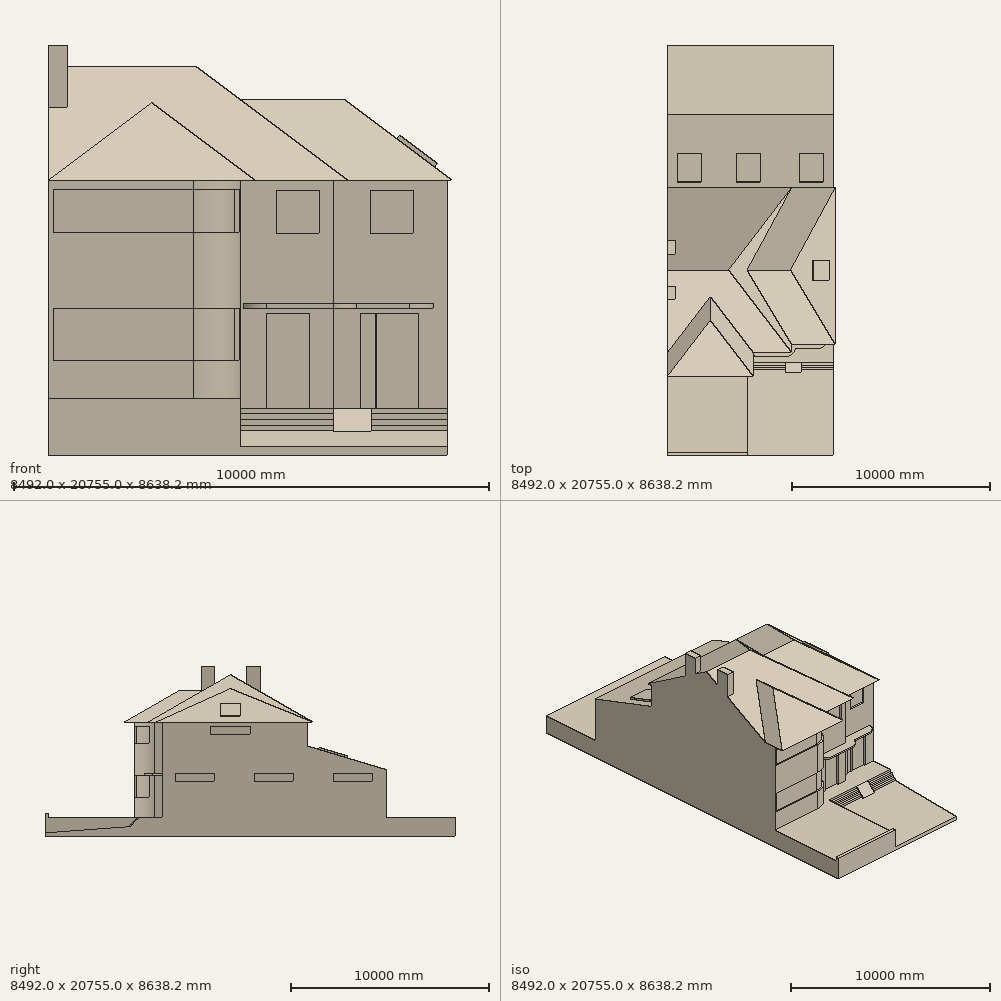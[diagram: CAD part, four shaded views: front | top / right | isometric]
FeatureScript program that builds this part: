
annotation { "Feature Type Name" : "Feature", "Feature Type Description" : "" }
export const myFeature = defineFeature(function(context is Context, id is Id, definition is map)
    precondition{}
    {
        {
            var Q0;
            Q0=qCreatedBy(makeId("Top.planeOp"),FACE);
            var sketch = newSketch(context, id + "F0", { "sketchPlane" : qUnion([Q0])});
            skLineSegment(sketch, "E0", {"start": v(0, -1400) * mm, "end": v(0, 11355) * mm});
            skLineSegment(sketch, "E1", {"start": v(0, 11355) * mm, "end": v(8392, 11355) * mm});
            skLineSegment(sketch, "E2", {"start": v(8392, 11355) * mm, "end": v(8392, 0) * mm});
            skLineSegment(sketch, "E3", {"start": v(8392, 0) * mm, "end": v(5992, 0) * mm});
            skLineSegment(sketch, "E4", {"start": v(5992, 0) * mm, "end": v(5992, -400) * mm});
            skLineSegment(sketch, "E5", {"start": v(5992, -400) * mm, "end": v(4042, -400) * mm});
            skLineSegment(sketch, "E6", {"start": v(0, -1400) * mm, "end": v(3042, -1400) * mm});
            skArc(sketch, "E7", {"start": v(3042, -1400) * mm, "mid": v(3749.1, -1107.1) * mm, "end": v(4042, -400) * mm});
            skSolve(sketch);
        }
        {
            var Q0;
            Q0=makeQuery(id+"F0.imprint","IMPRINT",FACE,{"disambiguationData":[TD([[makeQuery(id+"F0.imprint","IMPRINT",EDGE,{"derivedFrom":sQuery(id+"F0.wireOp",EDGE,"E0")}),-1.0]])]});
            extrude(context, id + "F1", {"entities" : qUnion([Q0]), "depth" : 4800 * mm});
        }
        {
            var Q0;
            Q0=makeQuery(id+"F1.opExtrude","CAP_FACE",FACE,{"disambiguationData":[OSD([sQuery(id+"F0.wireOp",EDGE,"E0"),sQuery(id+"F0.wireOp",EDGE,"E1"),sQuery(id+"F0.wireOp",EDGE,"E2"),sQuery(id+"F0.wireOp",EDGE,"E3"),sQuery(id+"F0.wireOp",EDGE,"E4"),sQuery(id+"F0.wireOp",EDGE,"E5"),sQuery(id+"F0.wireOp",EDGE,"E6"),sQuery(id+"F0.wireOp",EDGE,"E7")])],"isStart":false});
            var sketch = newSketch(context, id + "F2", { "sketchPlane" : qUnion([Q0])});
            skLineSegment(sketch, "E8.bottom", {"start": v(0, 11355) * mm, "end": v(8392, 11355) * mm});
            skLineSegment(sketch, "E8.top", {"start": v(0, 7355) * mm, "end": v(8392, 7355) * mm});
            skLineSegment(sketch, "E8.left", {"start": v(0, 11355) * mm, "end": v(0, 7355) * mm});
            skLineSegment(sketch, "E8.right", {"start": v(8392, 11355) * mm, "end": v(8392, 7355) * mm});
            skSolve(sketch);
        }
        {
            var Q0;
            Q0=makeQuery(id+"F2.imprint","IMPRINT",FACE,{"disambiguationData":[TD([[makeQuery(id+"F2.imprint","IMPRINT",EDGE,{"derivedFrom":sQuery(id+"F2.wireOp",EDGE,"E8.bottom")}),-1.0]])]});
            extrude(context, id + "F3", {"entities" : qUnion([Q0]), "operationType" : NewBodyOperationType.REMOVE, "oppositeDirection" : true, "depth" : 2400 * mm});
        }
        {
            var Q0;
            Q0=makeQuery(id+"F1.opExtrude","SWEPT_FACE",FACE,{"disambiguationData":[OSD([sQuery(id+"F0.wireOp",EDGE,"E2")])]});
            var sketch = newSketch(context, id + "F4", { "sketchPlane" : qUnion([Q0])});
            skLineSegment(sketch, "E9", {"start": v(11355, 2400) * mm, "end": v(7355, 3600) * mm});
            skLineSegment(sketch, "E10", {"start": v(7355, 3600) * mm, "end": v(7355, 2400) * mm});
            skLineSegment(sketch, "E11", {"start": v(7355, 2400) * mm, "end": v(11355, 2400) * mm});
            skSolve(sketch);
        }
        {
            var Q0;
            Q0=makeQuery(id+"F4.imprint","IMPRINT",FACE,{"disambiguationData":[TD([[makeQuery(id+"F4.imprint","IMPRINT",EDGE,{"derivedFrom":sQuery(id+"F4.wireOp",EDGE,"E9")}),1.0]])]});
            var Q1;
            Q1=makeQuery(id+"F1.opExtrude","SWEPT_FACE",FACE,{"disambiguationData":[OSD([sQuery(id+"F0.wireOp",EDGE,"E0")])]});
            extrude(context, id + "F5", {"entities" : qUnion([Q0]), "operationType" : NewBodyOperationType.ADD, "endBound" : BoundingType.UP_TO_SURFACE, "oppositeDirection" : true, "endBoundEntityFace" : qUnion([Q1]), "depth" : 25 * mm});
        }
        {
            var Q0;
            Q0=makeQuery(id+"F1.opExtrude","SWEPT_FACE",FACE,{"disambiguationData":[OSD([sQuery(id+"F0.wireOp",EDGE,"E4")])]});
            var sketch = newSketch(context, id + "F6", { "sketchPlane" : qUnion([Q0])});
            skLineSegment(sketch, "E12", {"start": v(-700, 4800) * mm, "end": v(3477.5, 7200) * mm});
            skLineSegment(sketch, "E13", {"start": v(3477.5, 7200) * mm, "end": v(7655, 4800) * mm});
            skLineSegment(sketch, "E14", {"start": v(7655, 4800) * mm, "end": v(-700, 4800) * mm});
            skSolve(sketch);
        }
        {
            var Q0;
            {var subQ0=sQuery(id+"F6.wireOp",EDGE,"E12");Q0=makeQuery(id+"F6.imprint","IMPRINT",FACE,{"disambiguationData":[TD([[makeQuery(id+"F6.imprint","IMPRINT",EDGE,{"derivedFrom":subQ0}),-1.0]])]});}
            var Q1;
            {var subQ0=sQuery(id+"F0.wireOp",EDGE,"E0");Q1=makeQuery(id+"F5.boolean.opBoolean","MERGE",FACE,{"derivedFrom":[makeQuery(id+"F1.opExtrude","SWEPT_FACE",FACE,{"disambiguationData":[OSD([subQ0])]}),makeQuery(id+"F5.opExtrude","CAP_FACE",FACE,{"disambiguationData":[OSD([subQ0])],"isStart":false})]});}
            extrude(context, id + "F7", {"entities" : qUnion([Q0]), "operationType" : NewBodyOperationType.ADD, "endBound" : BoundingType.UP_TO_SURFACE, "oppositeDirection" : true, "endBoundEntityFace" : qUnion([Q1]), "depth" : 25 * mm});
        }
        {
            var Q0;
            Q0 = qSketchRegion(id + "F6", true);
            extrude(context, id + "F8", {"entities" : qUnion([Q0]), "operationType" : NewBodyOperationType.ADD, "depth" : 300 * mm});
        }
        {
            var Q0;
            Q0=makeQuery(id+"F5.boolean.opBoolean","MERGE",FACE,{"derivedFrom":[makeQuery(id+"F1.opExtrude","SWEPT_FACE",FACE,{"disambiguationData":[OSD([sQuery(id+"F0.wireOp",EDGE,"E2")])]}),makeQuery(id+"F5.opExtrude","CAP_FACE",FACE,{"disambiguationData":[OSD([sQuery(id+"F4.wireOp",EDGE,"E9"),sQuery(id+"F4.wireOp",EDGE,"E10"),sQuery(id+"F4.wireOp",EDGE,"E11")])],"isStart":true})]});
            var sketch = newSketch(context, id + "F9", { "sketchPlane" : qUnion([Q0])});
            skLineSegment(sketch, "E15", {"start": v(-300, 4800) * mm, "end": v(3477.5, 6500) * mm});
            skLineSegment(sketch, "E16", {"start": v(3477.5, 6500) * mm, "end": v(7655, 4800) * mm});
            skLineSegment(sketch, "E17", {"start": v(7655, 4800) * mm, "end": v(-300, 4800) * mm});
            skLineSegment(sketch, "E18", {"start": v(3477.5, 6500) * mm, "end": v(3477.5, 7200) * mm, "construction": true});
            skSolve(sketch);
        }
        {
            var Q0;
            Q0=makeQuery(id+"F1.opExtrude","SWEPT_FACE",FACE,{"disambiguationData":[OSD([sQuery(id+"F0.wireOp",EDGE,"E6")])]});
            var sketch = newSketch(context, id + "F10", { "sketchPlane" : qUnion([Q0])});
            skLineSegment(sketch, "E19", {"start": v(6292, 4800) * mm, "end": v(2292, 7800) * mm});
            skLineSegment(sketch, "E20", {"start": v(2292, 7800) * mm, "end": v(6292, 7800) * mm});
            skLineSegment(sketch, "E21", {"start": v(6292, 7800) * mm, "end": v(6292, 4800) * mm});
            skSolve(sketch);
        }
        {
            var Q0;
            Q0=makeQuery(id+"F10.imprint","IMPRINT",FACE,{"disambiguationData":[TD([[makeQuery(id+"F10.imprint","IMPRINT",EDGE,{"derivedFrom":sQuery(id+"F10.wireOp",EDGE,"E19")}),-1.0]])]});
            extrude(context, id + "F11", {"entities" : qUnion([Q0]), "operationType" : NewBodyOperationType.REMOVE, "endBound" : BoundingType.THROUGH_ALL, "oppositeDirection" : true, "depth" : 25 * mm});
        }
        {
            var Q0;
            Q0=makeQuery(id+"F1.opExtrude","SWEPT_FACE",FACE,{"disambiguationData":[OSD([sQuery(id+"F0.wireOp",EDGE,"E6")])]});
            var sketch = newSketch(context, id + "F12", { "sketchPlane" : qUnion([Q0])});
            skLineSegment(sketch, "E22", {"start": v(0, 4800) * mm, "end": v(2171, 6428.25) * mm});
            skLineSegment(sketch, "E23", {"start": v(2171, 6428.25) * mm, "end": v(4342, 4800) * mm});
            skLineSegment(sketch, "E24", {"start": v(4342, 4800) * mm, "end": v(0, 4800) * mm});
            skSolve(sketch);
        }
        {
            var Q0;
            {var subQ6=sQuery(id+"F12.wireOp",EDGE,"E22");Q0=makeQuery(id+"F12.imprint","IMPRINT",FACE,{"disambiguationData":[TD([[makeQuery(id+"F12.imprint","IMPRINT",EDGE,{"derivedFrom":subQ6}),-1.0]])]});}
            extrude(context, id + "F13", {"entities" : qUnion([Q0]), "operationType" : NewBodyOperationType.ADD, "endBound" : BoundingType.UP_TO_NEXT, "oppositeDirection" : true, "depth" : 25 * mm});
        }
        {
            var Q0;
            Q0 = qSketchRegion(id + "F12", true);
            extrude(context, id + "F14", {"entities" : qUnion([Q0]), "operationType" : NewBodyOperationType.ADD, "depth" : 500 * mm});
        }
        {
            var Q0;
            {var subQ0=sQuery(id+"F0.wireOp",EDGE,"E0");Q0=makeQuery(id+"F7.boolean.opBoolean","MERGE",FACE,{"derivedFrom":[makeQuery(id+"F5.boolean.opBoolean","MERGE",FACE,{"derivedFrom":[makeQuery(id+"F1.opExtrude","SWEPT_FACE",FACE,{"disambiguationData":[OSD([subQ0])]}),makeQuery(id+"F5.opExtrude","CAP_FACE",FACE,{"disambiguationData":[OSD([subQ0])],"isStart":false})]}),makeQuery(id+"F7.opExtrude","CAP_FACE",FACE,{"disambiguationData":[OSD([subQ0])],"isStart":false})]});}
            var sketch = newSketch(context, id + "F15", { "sketchPlane" : qUnion([Q0])});
            skLineSegment(sketch, "E25", {"start": v(1900, 4800) * mm, "end": v(1900, 6428.25) * mm});
            skLineSegment(sketch, "E26", {"start": v(-934.17, 6428.25) * mm, "end": v(1900, 6428.25) * mm});
            skLineSegment(sketch, "E27", {"start": v(1900, 4800) * mm, "end": v(-934.17, 6428.25) * mm});
            skSolve(sketch);
        }
        {
            var Q0;
            Q0=makeQuery(id+"F15.imprint","IMPRINT",FACE,{"disambiguationData":[TD([[makeQuery(id+"F15.imprint","IMPRINT",EDGE,{"derivedFrom":sQuery(id+"F15.wireOp",EDGE,"E25")}),-1.0]])]});
            var Q1;
            Q1=makeQuery(id+"F15.imprint","IMPRINT",FACE,{"disambiguationData":[TD([[makeQuery(id+"F15.imprint","IMPRINT",EDGE,{"derivedFrom":sQuery(id+"F15.wireOp",EDGE,"E25")}),1.0]])]});
            extrude(context, id + "F16", {"entities" : qUnion([Q0, Q1]), "operationType" : NewBodyOperationType.REMOVE, "endBound" : BoundingType.THROUGH_ALL, "oppositeDirection" : true, "depth" : 25 * mm});
        }
        {
            var Q0;
            Q0=makeQuery(id+"F9.imprint","IMPRINT",FACE,{"disambiguationData":[TD([[makeQuery(id+"F9.imprint","IMPRINT",EDGE,{"derivedFrom":sQuery(id+"F9.wireOp",EDGE,"E15")}),-1.0]])]});
            extrude(context, id + "F17", {"entities" : qUnion([Q0]), "operationType" : NewBodyOperationType.ADD, "endBound" : BoundingType.UP_TO_NEXT, "oppositeDirection" : true, "depth" : 25 * mm});
        }
        {
            var Q0;
            Q0 = qSketchRegion(id + "F9", true);
            extrude(context, id + "F18", {"entities" : qUnion([Q0]), "operationType" : NewBodyOperationType.ADD, "depth" : 100 * mm});
        }
        {
            var Q0;
            Q0=makeQuery(id+"F13.boolean.opBoolean","MERGE",FACE,{"derivedFrom":[makeQuery(id+"F1.opExtrude","SWEPT_FACE",FACE,{"disambiguationData":[OSD([sQuery(id+"F0.wireOp",EDGE,"E6")])]}),makeQuery(id+"F13.opExtrude","CAP_FACE",FACE,{"disambiguationData":[OSD([sQuery(id+"F12.wireOp",EDGE,"E22"),sQuery(id+"F12.wireOp",EDGE,"E23"),sQuery(id+"F12.wireOp",EDGE,"E24")])],"isStart":true})]});
            var sketch = newSketch(context, id + "F19", { "sketchPlane" : qUnion([Q0])});
            skLineSegment(sketch, "E28", {"start": v(8492, 4800) * mm, "end": v(6225.33, 6500) * mm});
            skLineSegment(sketch, "E29", {"start": v(6225.33, 6500) * mm, "end": v(8492, 6500) * mm});
            skLineSegment(sketch, "E30", {"start": v(8492, 6500) * mm, "end": v(8492, 4800) * mm});
            skSolve(sketch);
        }
        {
            var Q0;
            Q0=makeQuery(id+"F19.imprint","IMPRINT",FACE,{"disambiguationData":[TD([[makeQuery(id+"F19.imprint","IMPRINT",EDGE,{"derivedFrom":sQuery(id+"F19.wireOp",EDGE,"E28")}),-1.0]])]});
            extrude(context, id + "F20", {"entities" : qUnion([Q0]), "operationType" : NewBodyOperationType.REMOVE, "endBound" : BoundingType.THROUGH_ALL, "oppositeDirection" : true, "depth" : 25 * mm});
        }
        {
            var Q0;
            Q0=makeQuery(id+"F17.boolean.opBoolean","MERGE",FACE,{"derivedFrom":[makeQuery(id+"F5.boolean.opBoolean","MERGE",FACE,{"derivedFrom":[makeQuery(id+"F1.opExtrude","SWEPT_FACE",FACE,{"disambiguationData":[OSD([sQuery(id+"F0.wireOp",EDGE,"E2")])]}),makeQuery(id+"F5.opExtrude","CAP_FACE",FACE,{"disambiguationData":[OSD([sQuery(id+"F4.wireOp",EDGE,"E9"),sQuery(id+"F4.wireOp",EDGE,"E10"),sQuery(id+"F4.wireOp",EDGE,"E11")])],"isStart":true})]}),makeQuery(id+"F17.opExtrude","CAP_FACE",FACE,{"disambiguationData":[OSD([sQuery(id+"F9.wireOp",EDGE,"E15"),sQuery(id+"F9.wireOp",EDGE,"E16"),sQuery(id+"F9.wireOp",EDGE,"E17")])],"isStart":true})]});
            var sketch = newSketch(context, id + "F21", { "sketchPlane" : qUnion([Q0])});
            skLineSegment(sketch, "E31.bottom", {"start": v(2477.5, 4600) * mm, "end": v(4477.5, 4600) * mm});
            skLineSegment(sketch, "E31.top", {"start": v(2477.5, 4200) * mm, "end": v(4477.5, 4200) * mm});
            skLineSegment(sketch, "E31.left", {"start": v(2477.5, 4600) * mm, "end": v(2477.5, 4200) * mm});
            skLineSegment(sketch, "E31.right", {"start": v(4477.5, 4600) * mm, "end": v(4477.5, 4200) * mm});
            skLineSegment(sketch, "E32", {"start": v(3477.5, 7200) * mm, "end": v(3477.5, 0) * mm, "construction": true});
            skPoint(sketch, "E33", {"position": v(3477.5, 4600) * mm});
            skLineSegment(sketch, "E34.bottom", {"start": v(677.5, 2200) * mm, "end": v(2677.5, 2200) * mm});
            skLineSegment(sketch, "E34.top", {"start": v(677.5, 1800) * mm, "end": v(2677.5, 1800) * mm});
            skLineSegment(sketch, "E34.left", {"start": v(677.5, 2200) * mm, "end": v(677.5, 1800) * mm});
            skLineSegment(sketch, "E34.right", {"start": v(2677.5, 2200) * mm, "end": v(2677.5, 1800) * mm});
            skLineSegment(sketch, "E35.bottom", {"start": v(4677.5, 2200) * mm, "end": v(6677.5, 2200) * mm});
            skLineSegment(sketch, "E35.top", {"start": v(4677.5, 1800) * mm, "end": v(6677.5, 1800) * mm});
            skLineSegment(sketch, "E35.left", {"start": v(4677.5, 2200) * mm, "end": v(4677.5, 1800) * mm});
            skLineSegment(sketch, "E35.right", {"start": v(6677.5, 2200) * mm, "end": v(6677.5, 1800) * mm});
            skLineSegment(sketch, "E36.bottom", {"start": v(8677.5, 2200) * mm, "end": v(10677.5, 2200) * mm});
            skLineSegment(sketch, "E36.top", {"start": v(8677.5, 1800) * mm, "end": v(10677.5, 1800) * mm});
            skLineSegment(sketch, "E36.left", {"start": v(8677.5, 2200) * mm, "end": v(8677.5, 1800) * mm});
            skLineSegment(sketch, "E36.right", {"start": v(10677.5, 2200) * mm, "end": v(10677.5, 1800) * mm});
            skSolve(sketch);
        }
        {
            var Q0;
            Q0=makeQuery(id+"F21.imprint","IMPRINT",FACE,{"disambiguationData":[TD([[makeQuery(id+"F21.imprint","IMPRINT",EDGE,{"derivedFrom":sQuery(id+"F21.wireOp",EDGE,"E35.bottom")}),-1.0]])]});
            var Q1;
            Q1=makeQuery(id+"F21.imprint","IMPRINT",FACE,{"disambiguationData":[TD([[makeQuery(id+"F21.imprint","IMPRINT",EDGE,{"derivedFrom":sQuery(id+"F21.wireOp",EDGE,"E34.bottom")}),-1.0]])]});
            var Q2;
            Q2=makeQuery(id+"F21.imprint","IMPRINT",FACE,{"disambiguationData":[TD([[makeQuery(id+"F21.imprint","IMPRINT",EDGE,{"derivedFrom":sQuery(id+"F21.wireOp",EDGE,"E31.bottom")}),-1.0]])]});
            var Q3;
            Q3=makeQuery(id+"F21.imprint","IMPRINT",FACE,{"disambiguationData":[TD([[makeQuery(id+"F21.imprint","IMPRINT",EDGE,{"derivedFrom":sQuery(id+"F21.wireOp",EDGE,"E36.bottom")}),-1.0]])]});
            extrude(context, id + "F22", {"entities" : qUnion([Q0, Q1, Q2, Q3]), "operationType" : NewBodyOperationType.REMOVE, "oppositeDirection" : true, "depth" : 100 * mm});
        }
        {
            var Q0;
            Q0=makeQuery(id+"F1.opExtrude","SWEPT_FACE",FACE,{"disambiguationData":[OSD([sQuery(id+"F0.wireOp",EDGE,"E3")])]});
            var sketch = newSketch(context, id + "F23", { "sketchPlane" : qUnion([Q0])});
            skLineSegment(sketch, "E37.bottom", {"start": v(6892, 0) * mm, "end": v(7792, 0) * mm});
            skLineSegment(sketch, "E37.top", {"start": v(6892, 2000) * mm, "end": v(7792, 2000) * mm});
            skLineSegment(sketch, "E37.left", {"start": v(6892, 0) * mm, "end": v(6892, 2000) * mm});
            skLineSegment(sketch, "E37.right", {"start": v(7792, 0) * mm, "end": v(7792, 2000) * mm});
            skLineSegment(sketch, "E38.bottom", {"start": v(6872, 0) * mm, "end": v(6572, 0) * mm});
            skLineSegment(sketch, "E38.top", {"start": v(6872, 2000) * mm, "end": v(6572, 2000) * mm});
            skLineSegment(sketch, "E38.left", {"start": v(6872, 0) * mm, "end": v(6872, 2000) * mm});
            skLineSegment(sketch, "E38.right", {"start": v(6572, 0) * mm, "end": v(6572, 2000) * mm});
            skLineSegment(sketch, "E39.bottom", {"start": v(6783.06, 4584.82) * mm, "end": v(7683.06, 4584.82) * mm});
            skLineSegment(sketch, "E39.top", {"start": v(6783.06, 3684.82) * mm, "end": v(7683.06, 3684.82) * mm});
            skLineSegment(sketch, "E39.left", {"start": v(6783.06, 4584.82) * mm, "end": v(6783.06, 3684.82) * mm});
            skLineSegment(sketch, "E39.right", {"start": v(7683.06, 4584.82) * mm, "end": v(7683.06, 3684.82) * mm});
            skLineSegment(sketch, "E40", {"start": v(7233.06, 4800) * mm, "end": v(7233.06, 4584.82) * mm, "construction": true});
            skPoint(sketch, "E40.startSnap0", {"position": v(7233.06, 4584.82) * mm});
            skSolve(sketch);
        }
        {
            var Q0;
            Q0=makeQuery(id+"F23.imprint","IMPRINT",FACE,{"disambiguationData":[TD([[makeQuery(id+"F23.imprint","IMPRINT",EDGE,{"derivedFrom":sQuery(id+"F23.wireOp",EDGE,"E39.bottom")}),-1.0]])]});
            var Q1;
            Q1=makeQuery(id+"F23.imprint","IMPRINT",FACE,{"disambiguationData":[TD([[makeQuery(id+"F23.imprint","IMPRINT",EDGE,{"derivedFrom":sQuery(id+"F23.wireOp",EDGE,"E37.bottom")}),-1.0]])]});
            var Q2;
            Q2=makeQuery(id+"F23.imprint","IMPRINT",FACE,{"disambiguationData":[TD([[makeQuery(id+"F23.imprint","IMPRINT",EDGE,{"derivedFrom":sQuery(id+"F23.wireOp",EDGE,"E38.bottom")}),-1.0]])]});
            extrude(context, id + "F24", {"entities" : qUnion([Q0, Q1, Q2]), "operationType" : NewBodyOperationType.REMOVE, "oppositeDirection" : true, "depth" : 100 * mm});
        }
        {
            var Q0;
            Q0=makeQuery(id+"F1.opExtrude","SWEPT_FACE",FACE,{"disambiguationData":[OSD([sQuery(id+"F0.wireOp",EDGE,"E5")])]});
            var sketch = newSketch(context, id + "F25", { "sketchPlane" : qUnion([Q0])});
            skLineSegment(sketch, "E41.bottom", {"start": v(4592, 0) * mm, "end": v(5492, 0) * mm});
            skLineSegment(sketch, "E41.top", {"start": v(4592, 2000) * mm, "end": v(5492, 2000) * mm});
            skLineSegment(sketch, "E41.left", {"start": v(4592, 0) * mm, "end": v(4592, 2000) * mm});
            skLineSegment(sketch, "E41.right", {"start": v(5492, 0) * mm, "end": v(5492, 2000) * mm});
            skLineSegment(sketch, "E42.bottom", {"start": v(4792, 4584.82) * mm, "end": v(5692, 4584.82) * mm});
            skLineSegment(sketch, "E42.top", {"start": v(4792, 3684.82) * mm, "end": v(5692, 3684.82) * mm});
            skLineSegment(sketch, "E42.left", {"start": v(4792, 4584.82) * mm, "end": v(4792, 3684.82) * mm});
            skLineSegment(sketch, "E42.right", {"start": v(5692, 4584.82) * mm, "end": v(5692, 3684.82) * mm});
            skSolve(sketch);
        }
        {
            var Q0;
            Q0=makeQuery(id+"F25.imprint","IMPRINT",FACE,{"disambiguationData":[TD([[makeQuery(id+"F25.imprint","IMPRINT",EDGE,{"derivedFrom":sQuery(id+"F25.wireOp",EDGE,"E41.bottom")}),-1.0]])]});
            var Q1;
            Q1=makeQuery(id+"F25.imprint","IMPRINT",FACE,{"disambiguationData":[TD([[makeQuery(id+"F25.imprint","IMPRINT",EDGE,{"derivedFrom":sQuery(id+"F25.wireOp",EDGE,"E42.bottom")}),-1.0]])]});
            extrude(context, id + "F26", {"entities" : qUnion([Q0, Q1]), "operationType" : NewBodyOperationType.REMOVE, "oppositeDirection" : true, "depth" : 100 * mm});
        }
        {
            var Q0;
            Q0=makeQuery(id+"F1.opExtrude","CAP_FACE",FACE,{"disambiguationData":[OSD([sQuery(id+"F0.wireOp",EDGE,"E0"),sQuery(id+"F0.wireOp",EDGE,"E1"),sQuery(id+"F0.wireOp",EDGE,"E2"),sQuery(id+"F0.wireOp",EDGE,"E3"),sQuery(id+"F0.wireOp",EDGE,"E4"),sQuery(id+"F0.wireOp",EDGE,"E5"),sQuery(id+"F0.wireOp",EDGE,"E6"),sQuery(id+"F0.wireOp",EDGE,"E7")])],"isStart":true});
            cPlane(context, id + "F27", {"entities" : qUnion([Q0]), "cplaneType" : CPlaneType.OFFSET, "offset" : 1000 * mm, "oppositeDirection" : true, "width" : 150 * mm, "height" : 150 * mm});
        }
        {
            var Q0;
            Q0=qCreatedBy(id+"F27.planeOp",FACE);
            var sketch = newSketch(context, id + "F28", { "sketchPlane" : qUnion([Q0])});
            skLineSegment(sketch, "E43", {"start": v(100, 1400) * mm, "end": v(100, 1300) * mm});
            skLineSegment(sketch, "E44", {"start": v(100, 1300) * mm, "end": v(3042, 1300) * mm});
            skArc(sketch, "E45", {"start": v(3913.42, 624.99) * mm, "mid": v(3593.14, 1111.5) * mm, "end": v(3042, 1300) * mm});
            skArc(sketch, "E46", {"start": v(4016.36, 624.99) * mm, "mid": v(3664.5, 1182.62) * mm, "end": v(3042, 1400) * mm});
            skLineSegment(sketch, "E47", {"start": v(100, 1400) * mm, "end": v(3042, 1400) * mm});
            skLineSegment(sketch, "E48", {"start": v(3913.42, 624.99) * mm, "end": v(4016.36, 624.99) * mm});
            skSolve(sketch);
        }
        {
            var Q0;
            Q0 = qSketchRegion(id + "F28", true);
            extrude(context, id + "F29", {"entities" : qUnion([Q0]), "operationType" : NewBodyOperationType.REMOVE, "oppositeDirection" : true, "depth" : 1100 * mm});
        }
        {
            var Q0;
            Q0=makeQuery(id+"F1.opExtrude","CAP_FACE",FACE,{"disambiguationData":[OSD([sQuery(id+"F0.wireOp",EDGE,"E0"),sQuery(id+"F0.wireOp",EDGE,"E1"),sQuery(id+"F0.wireOp",EDGE,"E2"),sQuery(id+"F0.wireOp",EDGE,"E3"),sQuery(id+"F0.wireOp",EDGE,"E4"),sQuery(id+"F0.wireOp",EDGE,"E5"),sQuery(id+"F0.wireOp",EDGE,"E6"),sQuery(id+"F0.wireOp",EDGE,"E7")])],"isStart":true});
            cPlane(context, id + "F30", {"entities" : qUnion([Q0]), "cplaneType" : CPlaneType.OFFSET, "offset" : 3700 * mm, "oppositeDirection" : true, "width" : 150 * mm, "height" : 150 * mm});
        }
        {
            var Q0;
            Q0=qCreatedBy(id+"F30.planeOp",FACE);
            var sketch = newSketch(context, id + "F31", { "sketchPlane" : qUnion([Q0])});
            skLineSegment(sketch, "E49.0", {"start": v(100, 1300) * mm, "end": v(3042, 1300) * mm});
            skArc(sketch, "E49.1", {"start": v(3913.42, 624.99) * mm, "mid": v(3593.14, 1111.5) * mm, "end": v(3042, 1300) * mm});
            skLineSegment(sketch, "E49.2", {"start": v(3913.42, 624.99) * mm, "end": v(4016.36, 624.99) * mm});
            skLineSegment(sketch, "E50.0", {"start": v(100, 1400) * mm, "end": v(100, 1300) * mm});
            skLineSegment(sketch, "E51.0", {"start": v(100, 1400) * mm, "end": v(3042, 1400) * mm});
            skArc(sketch, "E51.1", {"start": v(3042, 1400) * mm, "mid": v(3664.5, 1182.62) * mm, "end": v(4016.36, 624.99) * mm});
            skPoint(sketch, "E52.orphan", {"position": v(4042, 400) * mm});
            skPoint(sketch, "E53.orphan", {"position": v(0, 1400) * mm});
            skSolve(sketch);
        }
        {
            var Q0;
            Q0 = qSketchRegion(id + "F31", true);
            extrude(context, id + "F32", {"entities" : qUnion([Q0]), "operationType" : NewBodyOperationType.REMOVE, "oppositeDirection" : true, "depth" : 900 * mm});
        }
        {
            var Q0;
            Q0=makeQuery(id+"F29.boolean.opBoolean","COPY",FACE,{"derivedFrom":makeQuery(id+"F29.opExtrude","CAP_FACE",FACE,{"disambiguationData":[OSD([sQuery(id+"F28.wireOp",EDGE,"E43"),sQuery(id+"F28.wireOp",EDGE,"E44"),sQuery(id+"F28.wireOp",EDGE,"E45"),sQuery(id+"F28.wireOp",EDGE,"E46"),sQuery(id+"F28.wireOp",EDGE,"E47"),sQuery(id+"F28.wireOp",EDGE,"E48")])],"isStart":false})});
            var sketch = newSketch(context, id + "F33", { "sketchPlane" : qUnion([Q0])});
            skLineSegment(sketch, "E54", {"start": v(8092, 500) * mm, "end": v(8092, 0) * mm});
            skLineSegment(sketch, "E55", {"start": v(8092, 0) * mm, "end": v(5992, 0) * mm});
            skLineSegment(sketch, "E56", {"start": v(5992, 0) * mm, "end": v(5992, 400) * mm});
            skLineSegment(sketch, "E57", {"start": v(5992, 400) * mm, "end": v(4092, 400) * mm});
            skLineSegment(sketch, "E58", {"start": v(4092, 400) * mm, "end": v(4092, 900) * mm});
            skLineSegment(sketch, "E59", {"start": v(4092, 900) * mm, "end": v(5992, 900) * mm});
            skLineSegment(sketch, "E60", {"start": v(6481.9, 500) * mm, "end": v(8092, 500) * mm});
            skArc(sketch, "E61", {"start": v(6481.9, 500) * mm, "mid": v(6308.23, 787.3) * mm, "end": v(5992, 900) * mm});
            skSolve(sketch);
        }
        {
            var Q0;
            Q0=makeQuery(id+"F33.imprint","IMPRINT",FACE,{"disambiguationData":[TD([[makeQuery(id+"F33.imprint","IMPRINT",EDGE,{"derivedFrom":sQuery(id+"F33.wireOp",EDGE,"E54")}),-1.0]])]});
            extrude(context, id + "F34", {"entities" : qUnion([Q0]), "operationType" : NewBodyOperationType.ADD, "oppositeDirection" : true, "depth" : 100 * mm});
        }
        {
            var Q0;
            {var subQ0=sQuery(id+"F0.wireOp",EDGE,"E0");Q0=makeQuery(id+"F7.boolean.opBoolean","MERGE",FACE,{"derivedFrom":[makeQuery(id+"F5.boolean.opBoolean","MERGE",FACE,{"derivedFrom":[makeQuery(id+"F1.opExtrude","SWEPT_FACE",FACE,{"disambiguationData":[OSD([subQ0])]}),makeQuery(id+"F5.opExtrude","CAP_FACE",FACE,{"disambiguationData":[OSD([subQ0])],"isStart":false})]}),makeQuery(id+"F7.opExtrude","CAP_FACE",FACE,{"disambiguationData":[OSD([subQ0])],"isStart":false})]});}
            var sketch = newSketch(context, id + "F35", { "sketchPlane" : qUnion([Q0])});
            skLineSegment(sketch, "E62.bottom", {"start": v(-1977.5, 6338.24) * mm, "end": v(-2677.5, 6338.24) * mm});
            skLineSegment(sketch, "E62.top", {"start": v(-1977.5, 7638.24) * mm, "end": v(-2677.5, 7638.24) * mm});
            skLineSegment(sketch, "E62.left", {"start": v(-1977.5, 6338.24) * mm, "end": v(-1977.5, 7638.24) * mm});
            skLineSegment(sketch, "E62.right", {"start": v(-2677.5, 6338.24) * mm, "end": v(-2677.5, 7638.24) * mm});
            skLineSegment(sketch, "E63.bottom", {"start": v(-4977.5, 6338.24) * mm, "end": v(-4277.5, 6338.24) * mm});
            skLineSegment(sketch, "E63.top", {"start": v(-4977.5, 7638.24) * mm, "end": v(-4277.5, 7638.24) * mm});
            skLineSegment(sketch, "E63.left", {"start": v(-4977.5, 6338.24) * mm, "end": v(-4977.5, 7638.24) * mm});
            skLineSegment(sketch, "E63.right", {"start": v(-4277.5, 6338.24) * mm, "end": v(-4277.5, 7638.24) * mm});
            skSolve(sketch);
        }
        {
            var Q0;
            {var subQ0=sQuery(id+"F35.wireOp",EDGE,"E62.top");Q0=makeQuery(id+"F35.imprint","IMPRINT",FACE,{"disambiguationData":[TD([[makeQuery(id+"F35.imprint","IMPRINT",EDGE,{"derivedFrom":subQ0}),1.0]])]});}
            var Q1;
            {var subQ0=sQuery(id+"F35.wireOp",EDGE,"E63.top");Q1=makeQuery(id+"F35.imprint","IMPRINT",FACE,{"disambiguationData":[TD([[makeQuery(id+"F35.imprint","IMPRINT",EDGE,{"derivedFrom":subQ0}),-1.0]])]});}
            extrude(context, id + "F36", {"entities" : qUnion([Q0, Q1]), "operationType" : NewBodyOperationType.ADD, "oppositeDirection" : true, "depth" : 400 * mm});
        }
        {
            var Q0;
            Q0=makeQuery(id+"F34.opExtrude","SWEPT_EDGE",EDGE,{"disambiguationData":[OSD([sQuery(id+"F33.wireOp",EDGE,"E54"),sQuery(id+"F33.wireOp",EDGE,"E60")])]});
            var Q1;
            Q1=makeQuery(id+"F34.opExtrude","SWEPT_EDGE",EDGE,{"disambiguationData":[OSD([sQuery(id+"F33.wireOp",EDGE,"E58"),sQuery(id+"F33.wireOp",EDGE,"E59")])]});
            fillet(context, id + "F37", {"entities" : qUnion([Q0, Q1]), "radius" : 500 * mm, "tangentPropagation" : true, "allowEdgeOverflow" : false});
        }
        {
            var Q0;
            Q0=makeQuery(id+"F1.opExtrude","SWEPT_FACE",FACE,{"disambiguationData":[OSD([sQuery(id+"F0.wireOp",EDGE,"E1")])]});
            var sketch = newSketch(context, id + "F38", { "sketchPlane" : qUnion([Q0])});
            skLineSegment(sketch, "E64.bottom", {"start": v(-8152, 0) * mm, "end": v(-6252, 0) * mm});
            skLineSegment(sketch, "E64.top", {"start": v(-8152, 2300) * mm, "end": v(-6252, 2300) * mm});
            skLineSegment(sketch, "E64.left", {"start": v(-8152, 0) * mm, "end": v(-8152, 2300) * mm});
            skLineSegment(sketch, "E64.right", {"start": v(-6252, 0) * mm, "end": v(-6252, 2300) * mm});
            skSolve(sketch);
        }
        {
            var Q0;
            Q0=makeQuery(id+"F38.imprint","IMPRINT",FACE,{"disambiguationData":[TD([[makeQuery(id+"F38.imprint","IMPRINT",EDGE,{"derivedFrom":sQuery(id+"F38.wireOp",EDGE,"E64.bottom")}),-1.0]])]});
            extrude(context, id + "F39", {"entities" : qUnion([Q0]), "operationType" : NewBodyOperationType.REMOVE, "oppositeDirection" : true, "depth" : 2000 * mm});
        }
        {
            var Q0;
            Q0=makeQuery(id+"F1.opExtrude","SWEPT_FACE",FACE,{"disambiguationData":[OSD([sQuery(id+"F0.wireOp",EDGE,"E1")])]});
            var sketch = newSketch(context, id + "F40", { "sketchPlane" : qUnion([Q0])});
            skLineSegment(sketch, "E65", {"start": v(-850, 0) * mm, "end": v(-850, 2000) * mm});
            skLineSegment(sketch, "E66", {"start": v(-850, 2000) * mm, "end": v(-2088, 2000) * mm});
            skLineSegment(sketch, "E67", {"start": v(-5952, 2000) * mm, "end": v(-5952, 1000) * mm});
            skLineSegment(sketch, "E68", {"start": v(-5952, 1000) * mm, "end": v(-4714, 1000) * mm});
            skLineSegment(sketch, "E69", {"start": v(-2088, 2000) * mm, "end": v(-2088, 0) * mm});
            skLineSegment(sketch, "E70", {"start": v(-2088, 0) * mm, "end": v(-850, 0) * mm});
            skLineSegment(sketch, "E71", {"start": v(-4714, 2000) * mm, "end": v(-4714, 1000) * mm});
            skLineSegment(sketch, "E72.trimOffspring", {"start": v(-4714, 2000) * mm, "end": v(-5952, 2000) * mm});
            skLineSegment(sketch, "E73.bottom", {"start": v(-2138, 2000) * mm, "end": v(-3376, 2000) * mm});
            skLineSegment(sketch, "E73.top", {"start": v(-2138, 0) * mm, "end": v(-3376, 0) * mm});
            skLineSegment(sketch, "E73.left", {"start": v(-2138, 2000) * mm, "end": v(-2138, 0) * mm});
            skLineSegment(sketch, "E73.right", {"start": v(-3376, 2000) * mm, "end": v(-3376, 0) * mm});
            skLineSegment(sketch, "E74.bottom", {"start": v(-3426, 2000) * mm, "end": v(-4664, 2000) * mm});
            skLineSegment(sketch, "E74.top", {"start": v(-3426, 0) * mm, "end": v(-4664, 0) * mm});
            skLineSegment(sketch, "E74.left", {"start": v(-3426, 2000) * mm, "end": v(-3426, 0) * mm});
            skLineSegment(sketch, "E74.right", {"start": v(-4664, 2000) * mm, "end": v(-4664, 0) * mm});
            skSolve(sketch);
        }
        {
            var Q0;
            Q0=makeQuery(id+"F40.imprint","IMPRINT",FACE,{"disambiguationData":[TD([[makeQuery(id+"F40.imprint","IMPRINT",EDGE,{"derivedFrom":sQuery(id+"F40.wireOp",EDGE,"E65")}),1.0]])]});
            var Q1;
            Q1=makeQuery(id+"F40.imprint","IMPRINT",FACE,{"disambiguationData":[TD([[makeQuery(id+"F40.imprint","IMPRINT",EDGE,{"derivedFrom":sQuery(id+"F40.wireOp",EDGE,"E73.bottom")}),1.0]])]});
            var Q2;
            Q2=makeQuery(id+"F40.imprint","IMPRINT",FACE,{"disambiguationData":[TD([[makeQuery(id+"F40.imprint","IMPRINT",EDGE,{"derivedFrom":sQuery(id+"F40.wireOp",EDGE,"E74.bottom")}),1.0]])]});
            var Q3;
            Q3=makeQuery(id+"F40.imprint","IMPRINT",FACE,{"disambiguationData":[TD([[makeQuery(id+"F40.imprint","IMPRINT",EDGE,{"derivedFrom":sQuery(id+"F40.wireOp",EDGE,"E67")}),1.0]])]});
            extrude(context, id + "F41", {"entities" : qUnion([Q0, Q1, Q2, Q3]), "operationType" : NewBodyOperationType.REMOVE, "oppositeDirection" : true, "depth" : 100 * mm});
        }
        {
            var Q0;
            Q0=makeQuery(id+"F5.opExtrude","SWEPT_FACE",FACE,{"disambiguationData":[OSD([sQuery(id+"F4.wireOp",EDGE,"E9")])]});
            var sketch = newSketch(context, id + "F42", { "sketchPlane" : qUnion([Q0])});
            skLineSegment(sketch, "E75.bottom", {"start": v(7892, 6610.36) * mm, "end": v(6692, 6610.36) * mm});
            skLineSegment(sketch, "E75.top", {"start": v(7892, 8094.9) * mm, "end": v(6692, 8094.9) * mm});
            skLineSegment(sketch, "E75.left", {"start": v(7892, 6610.36) * mm, "end": v(7892, 8094.9) * mm});
            skLineSegment(sketch, "E75.right", {"start": v(6692, 6610.36) * mm, "end": v(6692, 8094.9) * mm});
            skLineSegment(sketch, "E76.bottom", {"start": v(500, 6610.36) * mm, "end": v(1700, 6610.36) * mm});
            skLineSegment(sketch, "E76.top", {"start": v(500, 8094.9) * mm, "end": v(1700, 8094.9) * mm});
            skLineSegment(sketch, "E76.left", {"start": v(500, 6610.36) * mm, "end": v(500, 8094.9) * mm});
            skLineSegment(sketch, "E76.right", {"start": v(1700, 6610.36) * mm, "end": v(1700, 8094.9) * mm});
            skLineSegment(sketch, "E77.bottom", {"start": v(4700, 6610.36) * mm, "end": v(3500, 6610.36) * mm});
            skLineSegment(sketch, "E77.top", {"start": v(4700, 8094.9) * mm, "end": v(3500, 8094.9) * mm});
            skLineSegment(sketch, "E77.left", {"start": v(4700, 6610.36) * mm, "end": v(4700, 8094.9) * mm});
            skLineSegment(sketch, "E77.right", {"start": v(3500, 6610.36) * mm, "end": v(3500, 8094.9) * mm});
            skSolve(sketch);
        }
        {
            var Q0;
            Q0=makeQuery(id+"F42.imprint","IMPRINT",FACE,{"disambiguationData":[TD([[makeQuery(id+"F42.imprint","IMPRINT",EDGE,{"derivedFrom":sQuery(id+"F42.wireOp",EDGE,"E75.bottom")}),-1.0]])]});
            var Q1;
            Q1=makeQuery(id+"F42.imprint","IMPRINT",FACE,{"disambiguationData":[TD([[makeQuery(id+"F42.imprint","IMPRINT",EDGE,{"derivedFrom":sQuery(id+"F42.wireOp",EDGE,"E76.bottom")}),1.0]])]});
            var Q2;
            Q2=makeQuery(id+"F42.imprint","IMPRINT",FACE,{"disambiguationData":[TD([[makeQuery(id+"F42.imprint","IMPRINT",EDGE,{"derivedFrom":sQuery(id+"F42.wireOp",EDGE,"E77.bottom")}),-1.0]])]});
            extrude(context, id + "F43", {"entities" : qUnion([Q0, Q1, Q2]), "operationType" : NewBodyOperationType.ADD, "depth" : 100 * mm});
        }
        {
            var Q0;
            Q0=makeQuery(id+"F20.boolean.opBoolean","COPY",FACE,{"derivedFrom":makeQuery(id+"F20.opExtrude","SWEPT_FACE",FACE,{"disambiguationData":[OSD([sQuery(id+"F19.wireOp",EDGE,"E28")])]})});
            var sketch = newSketch(context, id + "F44", { "sketchPlane" : qUnion([Q0])});
            skLineSegment(sketch, "E78.bottom", {"start": v(2463.6, 2964.03) * mm, "end": v(3463.6, 2964.03) * mm});
            skLineSegment(sketch, "E78.top", {"start": v(2463.6, 3964.03) * mm, "end": v(3463.6, 3964.03) * mm});
            skLineSegment(sketch, "E78.left", {"start": v(2463.6, 2964.03) * mm, "end": v(2463.6, 3964.03) * mm});
            skLineSegment(sketch, "E78.right", {"start": v(3463.6, 2964.03) * mm, "end": v(3463.6, 3964.03) * mm});
            skSolve(sketch);
        }
        {
            var Q0;
            Q0=makeQuery(id+"F44.imprint","IMPRINT",FACE,{"disambiguationData":[TD([[makeQuery(id+"F44.imprint","IMPRINT",EDGE,{"derivedFrom":sQuery(id+"F44.wireOp",EDGE,"E78.bottom")}),1.0]])]});
            extrude(context, id + "F45", {"entities" : qUnion([Q0]), "operationType" : NewBodyOperationType.ADD, "depth" : 100 * mm});
        }
        {
            var Q0;
            Q0=makeQuery(id+"F3.boolean.opBoolean","COPY",FACE,{"derivedFrom":makeQuery(id+"F3.opExtrude","SWEPT_FACE",FACE,{"disambiguationData":[OSD([sQuery(id+"F2.wireOp",EDGE,"E8.top")])]})});
            var sketch = newSketch(context, id + "F46", { "sketchPlane" : qUnion([Q0])});
            skLineSegment(sketch, "E79.bottom", {"start": v(-600, 4700) * mm, "end": v(-1800, 4700) * mm});
            skLineSegment(sketch, "E79.top", {"start": v(-600, 3800) * mm, "end": v(-1800, 3800) * mm});
            skLineSegment(sketch, "E79.left", {"start": v(-600, 4700) * mm, "end": v(-600, 3800) * mm});
            skLineSegment(sketch, "E79.right", {"start": v(-1800, 4700) * mm, "end": v(-1800, 3800) * mm});
            skLineSegment(sketch, "E80.bottom", {"start": v(-3800, 4632.38) * mm, "end": v(-4471.45, 4632.38) * mm});
            skLineSegment(sketch, "E80.top", {"start": v(-3800, 3732.38) * mm, "end": v(-4471.45, 3732.38) * mm});
            skLineSegment(sketch, "E80.left", {"start": v(-3800, 4632.38) * mm, "end": v(-3800, 3732.38) * mm});
            skLineSegment(sketch, "E80.right", {"start": v(-4471.45, 4632.38) * mm, "end": v(-4471.45, 3732.38) * mm});
            skLineSegment(sketch, "E81.bottom", {"start": v(-5271.45, 4632.38) * mm, "end": v(-5942.9, 4632.38) * mm});
            skLineSegment(sketch, "E81.top", {"start": v(-5271.45, 3732.38) * mm, "end": v(-5942.9, 3732.38) * mm});
            skLineSegment(sketch, "E81.left", {"start": v(-5271.45, 4632.38) * mm, "end": v(-5271.45, 3732.38) * mm});
            skLineSegment(sketch, "E81.right", {"start": v(-5942.9, 4632.38) * mm, "end": v(-5942.9, 3732.38) * mm});
            skSolve(sketch);
        }
        {
            var Q0;
            Q0=makeQuery(id+"F46.imprint","IMPRINT",FACE,{"disambiguationData":[TD([[makeQuery(id+"F46.imprint","IMPRINT",EDGE,{"derivedFrom":sQuery(id+"F46.wireOp",EDGE,"E81.bottom")}),1.0]])]});
            var Q1;
            Q1=makeQuery(id+"F46.imprint","IMPRINT",FACE,{"disambiguationData":[TD([[makeQuery(id+"F46.imprint","IMPRINT",EDGE,{"derivedFrom":sQuery(id+"F46.wireOp",EDGE,"E80.bottom")}),1.0]])]});
            var Q2;
            Q2=makeQuery(id+"F46.imprint","IMPRINT",FACE,{"disambiguationData":[TD([[makeQuery(id+"F46.imprint","IMPRINT",EDGE,{"derivedFrom":sQuery(id+"F46.wireOp",EDGE,"E79.bottom")}),1.0]])]});
            extrude(context, id + "F47", {"entities" : qUnion([Q0, Q1, Q2]), "operationType" : NewBodyOperationType.REMOVE, "oppositeDirection" : true, "depth" : 100 * mm});
        }
        {
            var Q0;
            Q0=makeQuery(id+"F1.opExtrude","CAP_FACE",FACE,{"disambiguationData":[OSD([sQuery(id+"F0.wireOp",EDGE,"E0"),sQuery(id+"F0.wireOp",EDGE,"E1"),sQuery(id+"F0.wireOp",EDGE,"E2"),sQuery(id+"F0.wireOp",EDGE,"E3"),sQuery(id+"F0.wireOp",EDGE,"E4"),sQuery(id+"F0.wireOp",EDGE,"E5"),sQuery(id+"F0.wireOp",EDGE,"E6"),sQuery(id+"F0.wireOp",EDGE,"E7")])],"isStart":true});
            var sketch = newSketch(context, id + "F48", { "sketchPlane" : qUnion([Q0])});
            skLineSegment(sketch, "E82.bottom", {"start": v(0, 5900) * mm, "end": v(8392, 5900) * mm});
            skLineSegment(sketch, "E82.top", {"start": v(0, -14855) * mm, "end": v(8392, -14855) * mm});
            skLineSegment(sketch, "E82.left", {"start": v(0, 5900) * mm, "end": v(0, -14855) * mm});
            skLineSegment(sketch, "E82.right", {"start": v(8392, 5900) * mm, "end": v(8392, -14855) * mm});
            skSolve(sketch);
        }
        {
            var Q0;
            Q0 = qSketchRegion(id + "F48", true);
            extrude(context, id + "F49", {"entities" : qUnion([Q0]), "operationType" : NewBodyOperationType.ADD, "depth" : 1000 * mm});
        }
        {
            var Q0;
            Q0=makeQuery(id+"F49.boolean.opBoolean","MERGE",FACE,{"derivedFrom":[makeQuery(id+"F17.boolean.opBoolean","MERGE",FACE,{"derivedFrom":[makeQuery(id+"F5.boolean.opBoolean","MERGE",FACE,{"derivedFrom":[makeQuery(id+"F1.opExtrude","SWEPT_FACE",FACE,{"disambiguationData":[OSD([sQuery(id+"F0.wireOp",EDGE,"E2")])]}),makeQuery(id+"F5.opExtrude","CAP_FACE",FACE,{"disambiguationData":[OSD([sQuery(id+"F4.wireOp",EDGE,"E9"),sQuery(id+"F4.wireOp",EDGE,"E10"),sQuery(id+"F4.wireOp",EDGE,"E11")])],"isStart":true})]}),makeQuery(id+"F17.opExtrude","CAP_FACE",FACE,{"disambiguationData":[OSD([sQuery(id+"F9.wireOp",EDGE,"E15"),sQuery(id+"F9.wireOp",EDGE,"E16"),sQuery(id+"F9.wireOp",EDGE,"E17")])],"isStart":true})]}),makeQuery(id+"F49.opExtrude","SWEPT_FACE",FACE,{"disambiguationData":[OSD([sQuery(id+"F48.wireOp",EDGE,"E82.right")])]})]});
            var sketch = newSketch(context, id + "F50", { "sketchPlane" : qUnion([Q0])});
            skLineSegment(sketch, "E83", {"start": v(-1200, 0) * mm, "end": v(-1200, -120) * mm});
            skLineSegment(sketch, "E84", {"start": v(-1200, -120) * mm, "end": v(-1320, -120) * mm});
            skLineSegment(sketch, "E85", {"start": v(-1320, -120) * mm, "end": v(-1320, -240) * mm});
            skLineSegment(sketch, "E86", {"start": v(-1320, -240) * mm, "end": v(-1440, -240) * mm});
            skLineSegment(sketch, "E87", {"start": v(-1440, -240) * mm, "end": v(-1440, -360) * mm});
            skLineSegment(sketch, "E88", {"start": v(-5900, -800) * mm, "end": v(-5900, 0) * mm});
            skLineSegment(sketch, "E89", {"start": v(-5900, 0) * mm, "end": v(-1200, 0) * mm});
            skLineSegment(sketch, "E90", {"start": v(-1440, -360) * mm, "end": v(-1560, -360) * mm});
            skLineSegment(sketch, "E91", {"start": v(-1560, -360) * mm, "end": v(-1560, -480) * mm});
            skLineSegment(sketch, "E92", {"start": v(-1560, -480) * mm, "end": v(-5900, -800) * mm});
            skSolve(sketch);
        }
        {
            var Q0;
            Q0=makeQuery(id+"F50.imprint","IMPRINT",FACE,{"disambiguationData":[TD([[makeQuery(id+"F50.imprint","IMPRINT",EDGE,{"derivedFrom":sQuery(id+"F50.wireOp",EDGE,"E83")}),-1.0]])]});
            var Q1;
            Q1=makeQuery(id+"F1.opExtrude","CAP_VERTEX",VERTEX,{"disambiguationData":[OSD([sQuery(id+"F0.wireOp",EDGE,"E5"),sQuery(id+"F0.wireOp",EDGE,"E7")])],"isStart":true});
            extrude(context, id + "F51", {"entities" : qUnion([Q0]), "operationType" : NewBodyOperationType.REMOVE, "endBound" : BoundingType.UP_TO_VERTEX, "oppositeDirection" : true, "endBoundEntityVertex" : qUnion([Q1]), "depth" : 25 * mm});
        }
        {
            var Q0;
            Q0=makeQuery(id+"F49.opExtrude","SWEPT_FACE",FACE,{"disambiguationData":[OSD([sQuery(id+"F48.wireOp",EDGE,"E82.bottom")])]});
            var sketch = newSketch(context, id + "F52", { "sketchPlane" : qUnion([Q0])});
            skLineSegment(sketch, "E93.bottom", {"start": v(0, 0) * mm, "end": v(4042, 0) * mm});
            skLineSegment(sketch, "E93.top", {"start": v(0, 200) * mm, "end": v(4042, 200) * mm});
            skLineSegment(sketch, "E93.left", {"start": v(0, 0) * mm, "end": v(0, 200) * mm});
            skLineSegment(sketch, "E93.right", {"start": v(4042, 0) * mm, "end": v(4042, 200) * mm});
            skSolve(sketch);
        }
        {
            var Q0;
            Q0=makeQuery(id+"F52.imprint","IMPRINT",FACE,{"disambiguationData":[TD([[makeQuery(id+"F52.imprint","IMPRINT",EDGE,{"derivedFrom":sQuery(id+"F52.wireOp",EDGE,"E93.bottom")}),1.0]])]});
            extrude(context, id + "F53", {"entities" : qUnion([Q0]), "operationType" : NewBodyOperationType.ADD, "oppositeDirection" : true, "depth" : 150 * mm});
        }
        {
            var Q0;
            {var subQ0=sQuery(id+"F0.wireOp",EDGE,"E5");var subQ1=sQuery(id+"F0.wireOp",EDGE,"E4");var subQ2=sQuery(id+"F0.wireOp",EDGE,"E3");Q0=makeQuery(id+"F34.boolean.opBoolean","SPLIT",FACE,{"disambiguationData":[TD([makeQuery(id+"F1.opExtrude","CAP_FACE",FACE,{"disambiguationData":[OSD([sQuery(id+"F0.wireOp",EDGE,"E0"),sQuery(id+"F0.wireOp",EDGE,"E1"),sQuery(id+"F0.wireOp",EDGE,"E2"),subQ2,subQ1,subQ0,sQuery(id+"F0.wireOp",EDGE,"E6"),sQuery(id+"F0.wireOp",EDGE,"E7")])],"isStart":true})])],"derivedFrom":makeQuery(id+"F7.boolean.opBoolean","MERGE",FACE,{"derivedFrom":[makeQuery(id+"F1.opExtrude","SWEPT_FACE",FACE,{"disambiguationData":[OSD([subQ1])]}),makeQuery(id+"F7.opExtrude","CAP_FACE",FACE,{"disambiguationData":[OSD([sQuery(id+"F6.wireOp",EDGE,"E12"),sQuery(id+"F6.wireOp",EDGE,"E13"),sQuery(id+"F6.wireOp",EDGE,"E14")])],"isStart":true})]})});}
            var sketch = newSketch(context, id + "F54", { "sketchPlane" : qUnion([Q0])});
            skLineSegment(sketch, "E94", {"start": v(-1200, 0) * mm, "end": v(-1689.55, -489.55) * mm});
            skLineSegment(sketch, "E95", {"start": v(-1689.55, -489.55) * mm, "end": v(-1200, -489.55) * mm});
            skLineSegment(sketch, "E96", {"start": v(-1200, -489.55) * mm, "end": v(-1200, 0) * mm});
            skSolve(sketch);
        }
        {
            var Q0;
            Q0=makeQuery(id+"F54.imprint","IMPRINT",FACE,{"disambiguationData":[TD([[makeQuery(id+"F54.imprint","IMPRINT",EDGE,{"derivedFrom":sQuery(id+"F54.wireOp",EDGE,"E94")}),1.0]])]});
            extrude(context, id + "F55", {"entities" : qUnion([Q0]), "operationType" : NewBodyOperationType.ADD, "depth" : 800 * mm});
        }
    });
